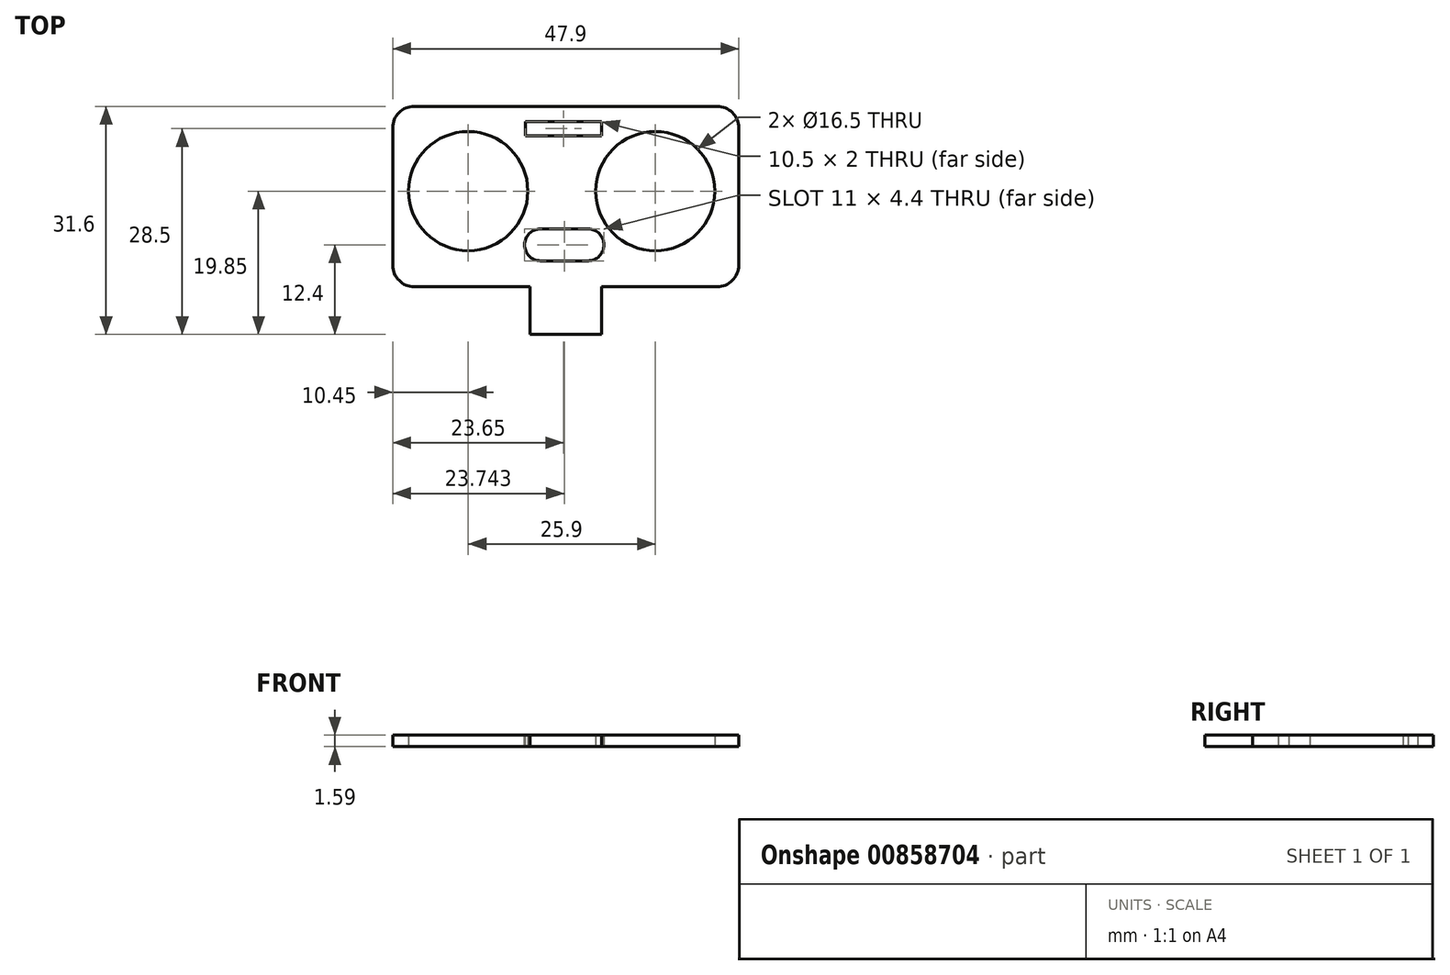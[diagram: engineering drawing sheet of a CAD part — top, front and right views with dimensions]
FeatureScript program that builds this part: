
annotation { "Feature Type Name" : "Feature", "Feature Type Description" : "" }
export const myFeature = defineFeature(function(context is Context, id is Id, definition is map)
    precondition{}
    {
        {
            assignVariable(context, id + "F0", {"name" : "holderT", "anyValue" : 1 / 16 * 25.4});
        }
        {
            assignVariable(context, id + "F1", {"name" : "crystalY", "anyValue" : 4.4});
        }
        {
            var Q0;
            Q0=qCreatedBy(makeId("Top.planeOp"),FACE);
            var sketch = newSketch(context, id + "F2", { "sketchPlane" : qUnion([Q0])});
            skCircle(sketch, "E0", {"center": v(-13.5, 13.25) * mm, "radius": 8.25 * mm});
            skCircle(sketch, "E1", {"center": v(12.4, 13.25) * mm, "radius": 8.25 * mm});
            skLineSegment(sketch, "E2.bottom", {"start": v(-23.95, 0) * mm, "end": v(23.95, 0) * mm});
            skLineSegment(sketch, "E2.top", {"start": v(-23.95, 25) * mm, "end": v(23.95, 25) * mm});
            skLineSegment(sketch, "E2.left", {"start": v(-23.95, 0) * mm, "end": v(-23.95, 25) * mm});
            skLineSegment(sketch, "E2.right", {"start": v(23.95, 0) * mm, "end": v(23.95, 25) * mm});
            skLineSegment(sketch, "E3", {"start": v(0, -10.52) * mm, "end": v(0, 5.44) * mm, "construction": true});
            skLineSegment(sketch, "E4.bottom", {"start": v(-4.95, 0) * mm, "end": v(4.95, 0) * mm});
            skLineSegment(sketch, "E4.top", {"start": v(-4.95, -6.6) * mm, "end": v(4.95, -6.6) * mm});
            skLineSegment(sketch, "E4.left", {"start": v(-4.95, 0) * mm, "end": v(-4.95, -6.6) * mm});
            skLineSegment(sketch, "E4.right", {"start": v(4.95, 0) * mm, "end": v(4.95, -6.6) * mm});
            skSolve(sketch);
        }
        {
            var Q0;
            Q0=qSketchRegion(id+"F2",true);
            extrude(context, id + "F3", {"entities" : qUnion([Q0]), "depth" : (getVariable(context, 'holderT')) * mm, "offsetDistance" : 25 * mm});
        }
        {
            var Q0;
            Q0=makeQuery(id+"F3.opExtrude","CAP_FACE",FACE,{"disambiguationData":[OSD([sQuery(id+"F2.wireOp",EDGE,"E0"),sQuery(id+"F2.wireOp",EDGE,"E1"),sQuery(id+"F2.wireOp",EDGE,"E2.bottom"),sQuery(id+"F2.wireOp",EDGE,"E2.top"),sQuery(id+"F2.wireOp",EDGE,"E2.left"),sQuery(id+"F2.wireOp",EDGE,"E2.right")])],"isStart":false});
            var sketch = newSketch(context, id + "F4", { "sketchPlane" : qUnion([Q0])});
            skLineSegment(sketch, "E5", {"start": v(-14.45, 0) * mm, "end": v(-14.45, 25) * mm, "construction": true});
            skLineSegment(sketch, "E6.bottom", {"start": v(-5.7, 3.6) * mm, "end": v(5.3, 3.6) * mm});
            skLineSegment(sketch, "E6.top", {"start": v(-5.7, 8) * mm, "end": v(5.3, 8) * mm});
            skLineSegment(sketch, "E6.left", {"start": v(-5.7, 3.6) * mm, "end": v(-5.7, 8) * mm});
            skLineSegment(sketch, "E6.right", {"start": v(5.3, 3.6) * mm, "end": v(5.3, 8) * mm});
            skLineSegment(sketch, "E7.bottom", {"start": v(-5.55, 22.9) * mm, "end": v(4.95, 22.9) * mm});
            skLineSegment(sketch, "E7.top", {"start": v(-5.55, 20.9) * mm, "end": v(4.95, 20.9) * mm});
            skLineSegment(sketch, "E7.left", {"start": v(-5.55, 22.9) * mm, "end": v(-5.55, 20.9) * mm});
            skLineSegment(sketch, "E7.right", {"start": v(4.95, 22.9) * mm, "end": v(4.95, 20.9) * mm});
            skSolve(sketch);
        }
        {
            var Q0;
            Q0=qSketchRegion(id+"F4",true);
            extrude(context, id + "F5", {"entities" : qUnion([Q0]), "operationType" : NewBodyOperationType.REMOVE, "endBound" : BoundingType.THROUGH_ALL, "oppositeDirection" : true, "depth" : 25 * mm, "offsetDistance" : 25 * mm});
        }
        {
            var Q0;
            Q0=makeQuery(id+"F3.opExtrude","SWEPT_EDGE",EDGE,{"disambiguationData":[OSD([sQuery(id+"F2.wireOp",EDGE,"E2.bottom"),sQuery(id+"F2.wireOp",EDGE,"E2.left")])]});
            var Q1;
            Q1=makeQuery(id+"F3.opExtrude","SWEPT_EDGE",EDGE,{"disambiguationData":[OSD([sQuery(id+"F2.wireOp",EDGE,"E2.top"),sQuery(id+"F2.wireOp",EDGE,"E2.left")])]});
            var Q2;
            Q2=makeQuery(id+"F3.opExtrude","SWEPT_EDGE",EDGE,{"disambiguationData":[OSD([sQuery(id+"F2.wireOp",EDGE,"E2.top"),sQuery(id+"F2.wireOp",EDGE,"E2.right")])]});
            var Q3;
            Q3=makeQuery(id+"F3.opExtrude","SWEPT_EDGE",EDGE,{"disambiguationData":[OSD([sQuery(id+"F2.wireOp",EDGE,"E2.bottom"),sQuery(id+"F2.wireOp",EDGE,"E2.right")])]});
            fillet(context, id + "F6", {"entities" : qUnion([Q0, Q1, Q2, Q3]), "radius" : 3 * mm, "tangentPropagation" : true, "allowEdgeOverflow" : false});
        }
        {
            var Q0;
            Q0=makeQuery(id+"F5.boolean.opBoolean","COPY",EDGE,{"derivedFrom":makeQuery(id+"F5.opExtrude","SWEPT_EDGE",EDGE,{"disambiguationData":[OSD([sQuery(id+"F2.wireOp",EDGE,"E2.bottom"),sQuery(id+"F4.wireOp",EDGE,"E6.bottom"),sQuery(id+"F4.wireOp",EDGE,"E6.left")])]})});
            var Q1;
            Q1=makeQuery(id+"F5.boolean.opBoolean","COPY",EDGE,{"derivedFrom":makeQuery(id+"F5.opExtrude","SWEPT_EDGE",EDGE,{"disambiguationData":[OSD([sQuery(id+"F4.wireOp",EDGE,"E6.top"),sQuery(id+"F4.wireOp",EDGE,"E6.left")])]})});
            var Q2;
            Q2=makeQuery(id+"F5.boolean.opBoolean","COPY",EDGE,{"derivedFrom":makeQuery(id+"F5.opExtrude","SWEPT_EDGE",EDGE,{"disambiguationData":[OSD([sQuery(id+"F2.wireOp",EDGE,"E2.bottom"),sQuery(id+"F4.wireOp",EDGE,"E6.bottom"),sQuery(id+"F4.wireOp",EDGE,"E6.right")])]})});
            var Q3;
            Q3=makeQuery(id+"F5.boolean.opBoolean","COPY",EDGE,{"derivedFrom":makeQuery(id+"F5.opExtrude","SWEPT_EDGE",EDGE,{"disambiguationData":[OSD([sQuery(id+"F4.wireOp",EDGE,"E6.top"),sQuery(id+"F4.wireOp",EDGE,"E6.right")])]})});
            fillet(context, id + "F7", {"entities" : qUnion([Q0, Q1, Q2, Q3]), "radius" : (getVariable(context, 'crystalY') / 2) * mm, "tangentPropagation" : true, "allowEdgeOverflow" : false});
        }
    });
